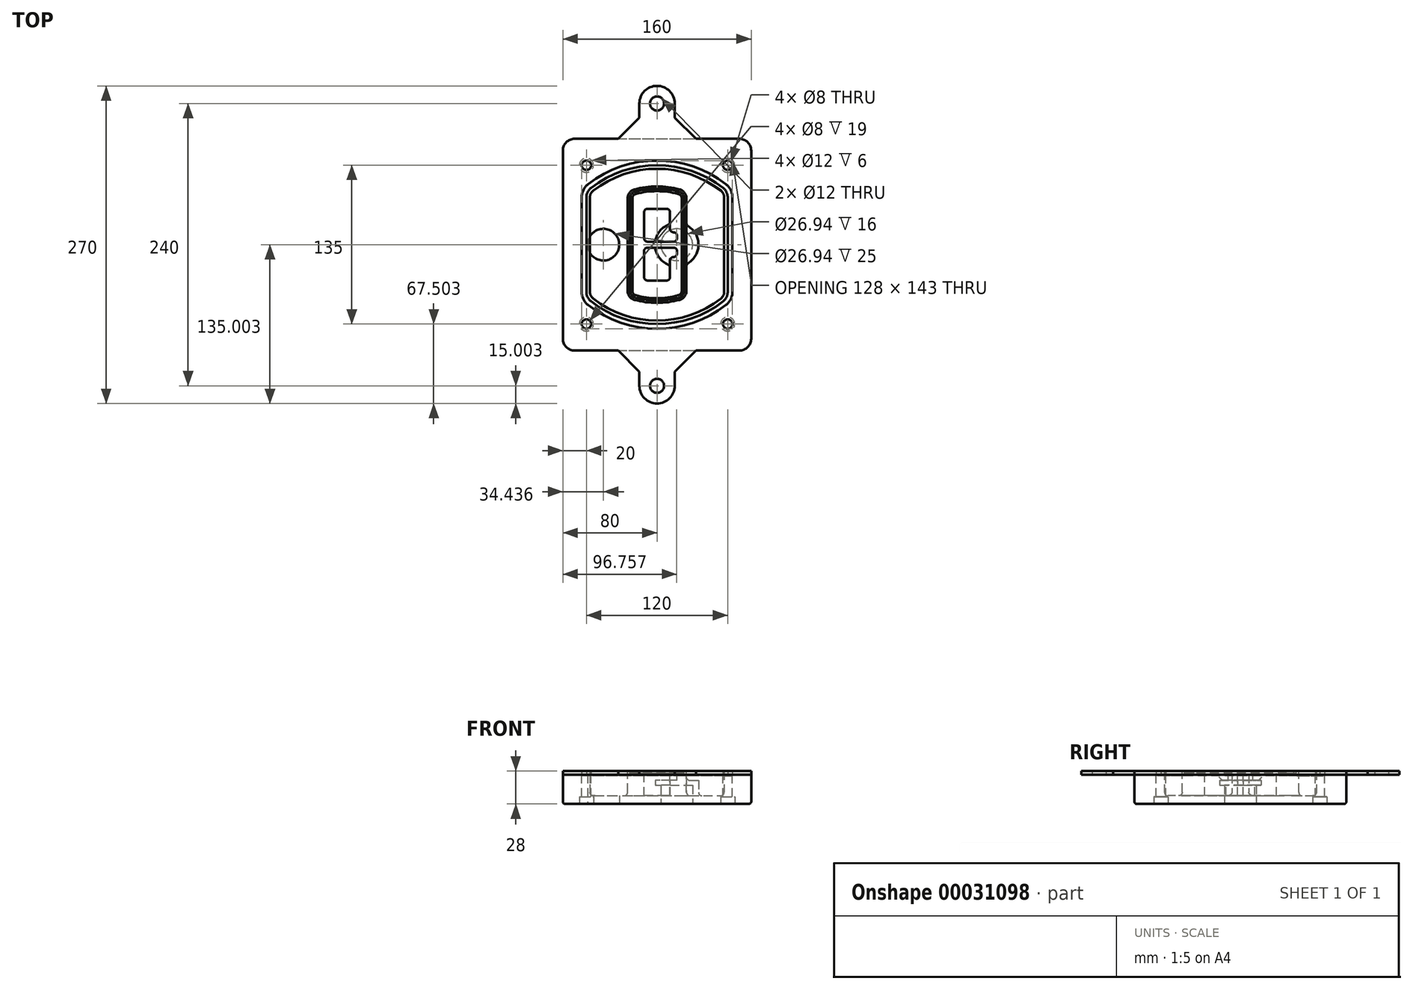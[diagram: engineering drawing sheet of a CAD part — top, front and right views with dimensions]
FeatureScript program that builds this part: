
annotation { "Feature Type Name" : "Feature", "Feature Type Description" : "" }
export const myFeature = defineFeature(function(context is Context, id is Id, definition is map)
    precondition{}
    {
        {
            var Q0;
            Q0=qCreatedBy(makeId("Top.planeOp"),FACE);
            var sketch = newSketch(context, id + "F0", { "sketchPlane" : qUnion([Q0])});
            skPoint(sketch, "E0.rect.middle", {"position": v(0, 0) * mm});
            skLineSegment(sketch, "E1.bottom", {"start": v(24.05, 28.38) * mm, "end": v(164.05, 28.38) * mm});
            skLineSegment(sketch, "E1.top", {"start": v(24.05, 208.38) * mm, "end": v(164.05, 208.38) * mm});
            skLineSegment(sketch, "E1.left", {"start": v(14.05, 38.38) * mm, "end": v(14.05, 198.38) * mm});
            skLineSegment(sketch, "E1.right", {"start": v(174.05, 38.38) * mm, "end": v(174.05, 198.38) * mm});
            skLineSegment(sketch, "E2", {"start": v(14.05, 208.38) * mm, "end": v(174.05, 28.38) * mm, "construction": true});
            skLineSegment(sketch, "E3", {"start": v(174.05, 208.38) * mm, "end": v(14.05, 28.38) * mm, "construction": true});
            skCircle(sketch, "E4", {"center": v(34.05, 185.88) * mm, "radius": 4 * mm});
            skCircle(sketch, "E5", {"center": v(154.05, 185.88) * mm, "radius": 4 * mm});
            skCircle(sketch, "E6", {"center": v(154.05, 50.88) * mm, "radius": 4 * mm});
            skCircle(sketch, "E7", {"center": v(34.05, 50.88) * mm, "radius": 4 * mm});
            skLineSegment(sketch, "E8", {"start": v(34.05, 185.88) * mm, "end": v(154.05, 185.88) * mm, "construction": true});
            skLineSegment(sketch, "E9", {"start": v(154.05, 185.88) * mm, "end": v(154.05, 50.88) * mm, "construction": true});
            skLineSegment(sketch, "E10", {"start": v(154.05, 50.88) * mm, "end": v(34.05, 50.88) * mm, "construction": true});
            skLineSegment(sketch, "E11", {"start": v(34.05, 50.88) * mm, "end": v(34.05, 185.88) * mm, "construction": true});
            skLineSegment(sketch, "E12", {"start": v(34.05, 158.68) * mm, "end": v(34.05, 78.09) * mm});
            skLineSegment(sketch, "E13", {"start": v(154.05, 158.68) * mm, "end": v(154.05, 78.09) * mm});
            skArc(sketch, "E14", {"start": v(150.2, 166.56) * mm, "mid": v(94.05, 185.88) * mm, "end": v(37.9, 166.56) * mm});
            skArc(sketch, "E15", {"start": v(37.9, 70.2) * mm, "mid": v(94.05, 50.88) * mm, "end": v(150.2, 70.2) * mm});
            skLineSegment(sketch, "E16", {"start": v(34.05, 118.38) * mm, "end": v(154.05, 118.38) * mm, "construction": true});
            skPoint(sketch, "E17.visualSharp", {"position": v(34.05, 73.38) * mm});
            skArc(sketch, "E17.filletArc", {"start": v(34.05, 78.09) * mm, "mid": v(35.06, 73.7) * mm, "end": v(37.9, 70.2) * mm});
            skPoint(sketch, "E18.visualSharp", {"position": v(34.05, 163.38) * mm});
            skArc(sketch, "E18.filletArc", {"start": v(37.9, 166.56) * mm, "mid": v(35.06, 163.06) * mm, "end": v(34.05, 158.68) * mm});
            skPoint(sketch, "E19.visualSharp", {"position": v(154.05, 163.38) * mm});
            skArc(sketch, "E19.filletArc", {"start": v(154.05, 158.68) * mm, "mid": v(153.04, 163.06) * mm, "end": v(150.2, 166.56) * mm});
            skPoint(sketch, "E20.visualSharp", {"position": v(154.05, 73.38) * mm});
            skArc(sketch, "E20.filletArc", {"start": v(150.2, 70.2) * mm, "mid": v(153.04, 73.7) * mm, "end": v(154.05, 78.09) * mm});
            skPoint(sketch, "E21.visualSharp", {"position": v(14.05, 208.38) * mm});
            skArc(sketch, "E21.filletArc", {"start": v(24.05, 208.38) * mm, "mid": v(16.98, 205.45) * mm, "end": v(14.05, 198.38) * mm});
            skPoint(sketch, "E22.visualSharp", {"position": v(174.05, 208.38) * mm});
            skArc(sketch, "E22.filletArc", {"start": v(174.05, 198.38) * mm, "mid": v(171.12, 205.45) * mm, "end": v(164.05, 208.38) * mm});
            skPoint(sketch, "E23.visualSharp", {"position": v(174.05, 28.38) * mm});
            skArc(sketch, "E23.filletArc", {"start": v(164.05, 28.38) * mm, "mid": v(171.12, 31.31) * mm, "end": v(174.05, 38.38) * mm});
            skPoint(sketch, "E24.visualSharp", {"position": v(14.05, 28.38) * mm});
            skArc(sketch, "E24.filletArc", {"start": v(14.05, 38.38) * mm, "mid": v(16.98, 31.31) * mm, "end": v(24.05, 28.38) * mm});
            skArc(sketch, "E25.0", {"start": v(151.05, 158.68) * mm, "mid": v(150.34, 161.75) * mm, "end": v(148.36, 164.2) * mm});
            skLineSegment(sketch, "E25.1", {"start": v(151.05, 158.68) * mm, "end": v(151.05, 78.09) * mm});
            skArc(sketch, "E25.2", {"start": v(148.36, 72.57) * mm, "mid": v(150.34, 75.02) * mm, "end": v(151.05, 78.09) * mm});
            skArc(sketch, "E25.3", {"start": v(39.74, 72.57) * mm, "mid": v(94.05, 53.88) * mm, "end": v(148.36, 72.57) * mm});
            skArc(sketch, "E25.4", {"start": v(37.05, 78.09) * mm, "mid": v(37.76, 75.02) * mm, "end": v(39.74, 72.57) * mm});
            skArc(sketch, "E25.5", {"start": v(148.36, 164.2) * mm, "mid": v(94.05, 182.88) * mm, "end": v(39.74, 164.2) * mm});
            skLineSegment(sketch, "E25.6", {"start": v(37.05, 158.68) * mm, "end": v(37.05, 78.09) * mm});
            skArc(sketch, "E25.7", {"start": v(39.74, 164.2) * mm, "mid": v(37.76, 161.75) * mm, "end": v(37.05, 158.68) * mm});
            skArc(sketch, "E26.0", {"start": v(35.43, 169.71) * mm, "mid": v(31.47, 164.82) * mm, "end": v(30.05, 158.68) * mm});
            skArc(sketch, "E26.1", {"start": v(152.67, 169.71) * mm, "mid": v(94.05, 189.88) * mm, "end": v(35.43, 169.71) * mm});
            skArc(sketch, "E26.2", {"start": v(158.05, 158.68) * mm, "mid": v(156.63, 164.82) * mm, "end": v(152.67, 169.71) * mm});
            skLineSegment(sketch, "E26.3", {"start": v(158.05, 158.68) * mm, "end": v(158.05, 78.09) * mm});
            skArc(sketch, "E26.4", {"start": v(152.67, 67.05) * mm, "mid": v(156.63, 71.95) * mm, "end": v(158.05, 78.09) * mm});
            skLineSegment(sketch, "E26.5", {"start": v(30.05, 158.68) * mm, "end": v(30.05, 78.09) * mm});
            skArc(sketch, "E26.6", {"start": v(35.43, 67.05) * mm, "mid": v(94.05, 46.88) * mm, "end": v(152.67, 67.05) * mm});
            skArc(sketch, "E26.7", {"start": v(30.05, 78.09) * mm, "mid": v(31.47, 71.95) * mm, "end": v(35.43, 67.05) * mm});
            skSolve(sketch);
        }
        {
            var Q0;
            Q0=makeQuery(id+"F0.imprint","IMPRINT",FACE,{"disambiguationData":[TD([[makeQuery(id+"F0.imprint","IMPRINT",EDGE,{"derivedFrom":sQuery(id+"F0.wireOp",EDGE,"E1.bottom")}),1.0]])]});
            var Q1;
            Q1=makeQuery(id+"F0.imprint","IMPRINT",FACE,{"disambiguationData":[TD([[makeQuery(id+"F0.imprint","IMPRINT",EDGE,{"derivedFrom":sQuery(id+"F0.wireOp",EDGE,"E12")}),1.0]])]});
            var Q2;
            Q2=makeQuery(id+"F0.imprint","IMPRINT",FACE,{"disambiguationData":[TD([[makeQuery(id+"F0.imprint","IMPRINT",EDGE,{"derivedFrom":sQuery(id+"F0.wireOp",EDGE,"E25.0")}),1.0]])]});
            var Q3;
            Q3=makeQuery(id+"F0.imprint","IMPRINT",FACE,{"disambiguationData":[TD([[makeQuery(id+"F0.imprint","IMPRINT",EDGE,{"derivedFrom":sQuery(id+"F0.wireOp",EDGE,"E12")}),-1.0]])]});
            extrude(context, id + "F1", {"entities" : qUnion([Q0, Q1, Q2, Q3]), "oppositeDirection" : true, "depth" : 25 * mm});
        }
        {
            var Q0;
            Q0=makeQuery(id+"F0.imprint","IMPRINT",FACE,{"disambiguationData":[TD([[makeQuery(id+"F0.imprint","IMPRINT",EDGE,{"derivedFrom":sQuery(id+"F0.wireOp",EDGE,"E12")}),1.0]])]});
            extrude(context, id + "F2", {"entities" : qUnion([Q0]), "operationType" : NewBodyOperationType.ADD, "depth" : 3 * mm});
        }
        {
            var Q0;
            Q0=makeQuery(id+"F0.imprint","IMPRINT",FACE,{"disambiguationData":[TD([[makeQuery(id+"F0.imprint","IMPRINT",EDGE,{"derivedFrom":sQuery(id+"F0.wireOp",EDGE,"E12")}),-1.0]])]});
            extrude(context, id + "F3", {"entities" : qUnion([Q0]), "operationType" : NewBodyOperationType.REMOVE, "oppositeDirection" : true, "depth" : 1 * mm});
        }
        {
            var Q0;
            Q0=makeQuery(id+"F0.imprint","IMPRINT",FACE,{"disambiguationData":[TD([[makeQuery(id+"F0.imprint","IMPRINT",EDGE,{"derivedFrom":sQuery(id+"F0.wireOp",EDGE,"E25.0")}),1.0]])]});
            extrude(context, id + "F4", {"entities" : qUnion([Q0]), "operationType" : NewBodyOperationType.REMOVE, "oppositeDirection" : true, "depth" : 18 * mm});
        }
        {
            var Q0;
            Q0=makeQuery(id+"F2.opExtrude","CAP_FACE",FACE,{"disambiguationData":[OSD([sQuery(id+"F0.wireOp",EDGE,"E12"),sQuery(id+"F0.wireOp",EDGE,"E13"),sQuery(id+"F0.wireOp",EDGE,"E14"),sQuery(id+"F0.wireOp",EDGE,"E15"),sQuery(id+"F0.wireOp",EDGE,"E17.filletArc"),sQuery(id+"F0.wireOp",EDGE,"E18.filletArc"),sQuery(id+"F0.wireOp",EDGE,"E19.filletArc"),sQuery(id+"F0.wireOp",EDGE,"E20.filletArc"),sQuery(id+"F0.wireOp",EDGE,"E25.0"),sQuery(id+"F0.wireOp",EDGE,"E25.1"),sQuery(id+"F0.wireOp",EDGE,"E25.2"),sQuery(id+"F0.wireOp",EDGE,"E25.3"),sQuery(id+"F0.wireOp",EDGE,"E25.4"),sQuery(id+"F0.wireOp",EDGE,"E25.5"),sQuery(id+"F0.wireOp",EDGE,"E25.6"),sQuery(id+"F0.wireOp",EDGE,"E25.7")])],"isStart":false});
            var sketch = newSketch(context, id + "F5", { "sketchPlane" : qUnion([Q0])});
            skArc(sketch, "E27.0", {"start": v(74.97, 71.41) * mm, "mid": v(94.05, 68.88) * mm, "end": v(113.13, 71.41) * mm});
            skArc(sketch, "E28.0", {"start": v(113.13, 165.35) * mm, "mid": v(94.05, 167.88) * mm, "end": v(74.97, 165.35) * mm});
            skLineSegment(sketch, "E29", {"start": v(69.05, 157.63) * mm, "end": v(69.05, 79.14) * mm});
            skLineSegment(sketch, "E30", {"start": v(119.05, 157.63) * mm, "end": v(119.05, 79.14) * mm});
            skLineSegment(sketch, "E31", {"start": v(69.05, 163.48) * mm, "end": v(119.05, 163.48) * mm, "construction": true});
            skLineSegment(sketch, "E32", {"start": v(69.05, 73.28) * mm, "end": v(119.05, 73.28) * mm, "construction": true});
            skPoint(sketch, "E33.visualSharp", {"position": v(69.05, 163.48) * mm});
            skArc(sketch, "E33.filletArc", {"start": v(74.97, 165.35) * mm, "mid": v(70.7, 162.5) * mm, "end": v(69.05, 157.63) * mm});
            skPoint(sketch, "E34.visualSharp", {"position": v(119.05, 163.48) * mm});
            skArc(sketch, "E34.filletArc", {"start": v(119.05, 157.63) * mm, "mid": v(117.4, 162.5) * mm, "end": v(113.13, 165.35) * mm});
            skPoint(sketch, "E35.visualSharp", {"position": v(119.05, 73.28) * mm});
            skArc(sketch, "E35.filletArc", {"start": v(113.13, 71.41) * mm, "mid": v(117.4, 74.27) * mm, "end": v(119.05, 79.14) * mm});
            skPoint(sketch, "E36.visualSharp", {"position": v(69.05, 73.28) * mm});
            skArc(sketch, "E36.filletArc", {"start": v(69.05, 79.14) * mm, "mid": v(70.7, 74.27) * mm, "end": v(74.97, 71.41) * mm});
            skArc(sketch, "E37.0", {"start": v(148.36, 164.2) * mm, "mid": v(94.05, 182.88) * mm, "end": v(39.74, 164.2) * mm});
            skArc(sketch, "E37.1", {"start": v(39.74, 164.2) * mm, "mid": v(37.76, 161.75) * mm, "end": v(37.05, 158.68) * mm});
            skLineSegment(sketch, "E37.2", {"start": v(37.05, 158.68) * mm, "end": v(37.05, 78.09) * mm});
            skArc(sketch, "E37.3", {"start": v(37.05, 78.09) * mm, "mid": v(37.76, 75.02) * mm, "end": v(39.74, 72.57) * mm});
            skArc(sketch, "E37.4", {"start": v(39.74, 72.57) * mm, "mid": v(94.05, 53.88) * mm, "end": v(148.36, 72.57) * mm});
            skArc(sketch, "E37.5", {"start": v(148.36, 72.57) * mm, "mid": v(150.34, 75.02) * mm, "end": v(151.05, 78.09) * mm});
            skLineSegment(sketch, "E37.6", {"start": v(151.05, 158.68) * mm, "end": v(151.05, 78.09) * mm});
            skArc(sketch, "E37.7", {"start": v(151.05, 158.68) * mm, "mid": v(150.34, 161.75) * mm, "end": v(148.36, 164.2) * mm});
            skLineSegment(sketch, "E38.0", {"start": v(117.05, 157.63) * mm, "end": v(117.05, 79.14) * mm});
            skArc(sketch, "E38.1", {"start": v(112.61, 73.34) * mm, "mid": v(115.81, 75.49) * mm, "end": v(117.05, 79.14) * mm});
            skArc(sketch, "E38.2", {"start": v(75.49, 73.34) * mm, "mid": v(94.05, 70.88) * mm, "end": v(112.61, 73.34) * mm});
            skArc(sketch, "E38.3", {"start": v(71.05, 79.14) * mm, "mid": v(72.29, 75.49) * mm, "end": v(75.49, 73.34) * mm});
            skLineSegment(sketch, "E38.4", {"start": v(71.05, 157.63) * mm, "end": v(71.05, 79.14) * mm});
            skArc(sketch, "E38.5", {"start": v(117.05, 157.63) * mm, "mid": v(115.81, 161.28) * mm, "end": v(112.61, 163.42) * mm});
            skArc(sketch, "E38.6", {"start": v(75.49, 163.42) * mm, "mid": v(72.29, 161.28) * mm, "end": v(71.05, 157.63) * mm});
            skArc(sketch, "E38.7", {"start": v(112.61, 163.42) * mm, "mid": v(94.05, 165.88) * mm, "end": v(75.49, 163.42) * mm});
            skArc(sketch, "E39.0", {"start": v(115.05, 157.63) * mm, "mid": v(114.23, 160.06) * mm, "end": v(112.1, 161.5) * mm});
            skLineSegment(sketch, "E39.1", {"start": v(115.05, 157.63) * mm, "end": v(115.05, 79.14) * mm});
            skArc(sketch, "E39.2", {"start": v(112.1, 75.27) * mm, "mid": v(114.23, 76.7) * mm, "end": v(115.05, 79.14) * mm});
            skArc(sketch, "E39.3", {"start": v(76, 75.27) * mm, "mid": v(94.05, 72.88) * mm, "end": v(112.1, 75.27) * mm});
            skArc(sketch, "E39.4", {"start": v(73.05, 79.14) * mm, "mid": v(73.87, 76.7) * mm, "end": v(76, 75.27) * mm});
            skArc(sketch, "E39.5", {"start": v(112.1, 161.5) * mm, "mid": v(94.05, 163.88) * mm, "end": v(76, 161.5) * mm});
            skLineSegment(sketch, "E39.6", {"start": v(73.05, 157.63) * mm, "end": v(73.05, 79.14) * mm});
            skArc(sketch, "E39.7", {"start": v(76, 161.5) * mm, "mid": v(73.87, 160.06) * mm, "end": v(73.05, 157.63) * mm});
            skLineSegment(sketch, "E40", {"start": v(69.05, 118.38) * mm, "end": v(119.05, 118.38) * mm, "construction": true});
            skLineSegment(sketch, "E41", {"start": v(83.05, 123.88) * mm, "end": v(83.05, 145.88) * mm});
            skLineSegment(sketch, "E42", {"start": v(86.05, 148.88) * mm, "end": v(102.05, 148.88) * mm});
            skLineSegment(sketch, "E43", {"start": v(105.05, 145.88) * mm, "end": v(105.05, 131.88) * mm});
            skLineSegment(sketch, "E44", {"start": v(108.05, 128.88) * mm, "end": v(108.05, 128.88) * mm});
            skLineSegment(sketch, "E45", {"start": v(111.05, 125.88) * mm, "end": v(111.05, 123.88) * mm});
            skLineSegment(sketch, "E46", {"start": v(108.05, 120.88) * mm, "end": v(86.05, 120.88) * mm});
            skPoint(sketch, "E47.visualSharp", {"position": v(83.05, 148.88) * mm});
            skArc(sketch, "E47.filletArc", {"start": v(86.05, 148.88) * mm, "mid": v(83.93, 148) * mm, "end": v(83.05, 145.88) * mm});
            skPoint(sketch, "E48.visualSharp", {"position": v(105.05, 148.88) * mm});
            skArc(sketch, "E48.filletArc", {"start": v(105.05, 145.88) * mm, "mid": v(104.17, 148) * mm, "end": v(102.05, 148.88) * mm});
            skPoint(sketch, "E49.visualSharp", {"position": v(105.05, 128.88) * mm});
            skArc(sketch, "E49.filletArc", {"start": v(105.05, 131.88) * mm, "mid": v(105.93, 129.76) * mm, "end": v(108.05, 128.88) * mm});
            skPoint(sketch, "E50.visualSharp", {"position": v(111.05, 128.88) * mm});
            skArc(sketch, "E50.filletArc", {"start": v(111.05, 125.88) * mm, "mid": v(110.17, 128) * mm, "end": v(108.05, 128.88) * mm});
            skPoint(sketch, "E51.visualSharp", {"position": v(111.05, 120.88) * mm});
            skArc(sketch, "E51.filletArc", {"start": v(108.05, 120.88) * mm, "mid": v(110.17, 121.76) * mm, "end": v(111.05, 123.88) * mm});
            skPoint(sketch, "E52.visualSharp", {"position": v(83.05, 120.88) * mm});
            skArc(sketch, "E52.filletArc", {"start": v(83.05, 123.88) * mm, "mid": v(83.93, 121.76) * mm, "end": v(86.05, 120.88) * mm});
            skLineSegment(sketch, "E53.0.MirrorCS", {"start": v(108.05, 115.88) * mm, "end": v(86.05, 115.88) * mm});
            skArc(sketch, "E54.0.MirrorCS", {"start": v(83.05, 112.88) * mm, "mid": v(83.93, 115) * mm, "end": v(86.05, 115.88) * mm});
            skLineSegment(sketch, "E55.0.MirrorCS", {"start": v(83.05, 112.88) * mm, "end": v(83.05, 90.88) * mm});
            skArc(sketch, "E56.0.MirrorCS", {"start": v(86.05, 87.88) * mm, "mid": v(83.93, 88.76) * mm, "end": v(83.05, 90.88) * mm});
            skLineSegment(sketch, "E57.0.MirrorCS", {"start": v(86.05, 87.88) * mm, "end": v(102.05, 87.88) * mm});
            skArc(sketch, "E58.0.MirrorCS", {"start": v(105.05, 90.88) * mm, "mid": v(104.17, 88.76) * mm, "end": v(102.05, 87.88) * mm});
            skLineSegment(sketch, "E59.0.MirrorCS", {"start": v(105.05, 90.88) * mm, "end": v(105.05, 104.88) * mm});
            skArc(sketch, "E60.0.MirrorCS", {"start": v(105.05, 104.88) * mm, "mid": v(105.93, 107) * mm, "end": v(108.05, 107.88) * mm});
            skArc(sketch, "E61.0.MirrorCS", {"start": v(111.05, 110.88) * mm, "mid": v(110.17, 108.76) * mm, "end": v(108.05, 107.88) * mm});
            skLineSegment(sketch, "E62.0.MirrorCS", {"start": v(111.05, 110.88) * mm, "end": v(111.05, 112.88) * mm});
            skArc(sketch, "E63.0.MirrorCS", {"start": v(108.05, 115.88) * mm, "mid": v(110.17, 115) * mm, "end": v(111.05, 112.88) * mm});
            skSolve(sketch);
        }
        {
            var Q0;
            Q0=makeQuery(id+"F5.imprint","IMPRINT",FACE,{"disambiguationData":[TD([[makeQuery(id+"F5.imprint","IMPRINT",EDGE,{"derivedFrom":sQuery(id+"F5.wireOp",EDGE,"E27.0")}),1.0]])]});
            var Q1;
            Q1=makeQuery(id+"F5.imprint","IMPRINT",FACE,{"disambiguationData":[TD([[makeQuery(id+"F5.imprint","IMPRINT",EDGE,{"derivedFrom":sQuery(id+"F5.wireOp",EDGE,"E38.0")}),-1.0]])]});
            var Q2;
            Q2=makeQuery(id+"F5.imprint","IMPRINT",FACE,{"disambiguationData":[TD([[makeQuery(id+"F5.imprint","IMPRINT",EDGE,{"derivedFrom":sQuery(id+"F5.wireOp",EDGE,"E39.0")}),1.0]])]});
            extrude(context, id + "F6", {"entities" : qUnion([Q0, Q1, Q2]), "operationType" : NewBodyOperationType.ADD, "endBound" : BoundingType.UP_TO_NEXT, "oppositeDirection" : true, "depth" : 25 * mm});
        }
        {
            var Q0;
            Q0=makeQuery(id+"F5.imprint","IMPRINT",FACE,{"disambiguationData":[TD([[makeQuery(id+"F5.imprint","IMPRINT",EDGE,{"derivedFrom":sQuery(id+"F5.wireOp",EDGE,"E38.0")}),-1.0]])]});
            extrude(context, id + "F7", {"entities" : qUnion([Q0]), "operationType" : NewBodyOperationType.REMOVE, "oppositeDirection" : true, "depth" : 2 * mm});
        }
        {
            var Q0;
            Q0=makeQuery(id+"F1.opExtrude","CAP_FACE",FACE,{"disambiguationData":[OSD([sQuery(id+"F0.wireOp",EDGE,"E1.bottom"),sQuery(id+"F0.wireOp",EDGE,"E1.top"),sQuery(id+"F0.wireOp",EDGE,"E1.left"),sQuery(id+"F0.wireOp",EDGE,"E1.right"),sQuery(id+"F0.wireOp",EDGE,"E4"),sQuery(id+"F0.wireOp",EDGE,"E5"),sQuery(id+"F0.wireOp",EDGE,"E6"),sQuery(id+"F0.wireOp",EDGE,"E7"),sQuery(id+"F0.wireOp",EDGE,"E21.filletArc"),sQuery(id+"F0.wireOp",EDGE,"E22.filletArc"),sQuery(id+"F0.wireOp",EDGE,"E23.filletArc"),sQuery(id+"F0.wireOp",EDGE,"E24.filletArc")])],"isStart":false});
            var sketch = newSketch(context, id + "F8", { "sketchPlane" : qUnion([Q0])});
            skCircle(sketch, "E64", {"center": v(110.8, -118.38) * mm, "radius": 13.47 * mm});
            skCircle(sketch, "E65", {"center": v(48.49, -118.38) * mm, "radius": 13.47 * mm});
            skLineSegment(sketch, "E66", {"start": v(174.05, -118.38) * mm, "end": v(14.05, -118.38) * mm});
            skCircle(sketch, "E67", {"center": v(110.8, -118.38) * mm, "radius": 18.47 * mm});
            skCircle(sketch, "E68", {"center": v(154.05, -185.88) * mm, "radius": 6 * mm});
            skCircle(sketch, "E69", {"center": v(34.05, -185.88) * mm, "radius": 6 * mm});
            skCircle(sketch, "E70", {"center": v(34.05, -50.88) * mm, "radius": 6 * mm});
            skCircle(sketch, "E71", {"center": v(154.05, -50.88) * mm, "radius": 6 * mm});
            skSolve(sketch);
        }
        {
            var Q0;
            {var subQ1=sQuery(id+"F8.wireOp",EDGE,"E66");var subQ4=sQuery(id+"F8.wireOp",EDGE,"E64");var subQ6=makeQuery(id+"F8.imprint","INTERSECT",VERTEX,{"disambiguationData":[OD(0.0)],"derivedFrom":[subQ4,subQ1]});Q0=makeQuery(id+"F8.imprint","IMPRINT",FACE,{"disambiguationData":[TD([[makeQuery(id+"F8.imprint","IMPRINT",EDGE,{"disambiguationData":[TD([[subQ6,-1.0]])],"derivedFrom":subQ4}),-1.0]])]});}
            var Q1;
            {var subQ0=sQuery(id+"F8.wireOp",EDGE,"E66");var subQ1=sQuery(id+"F8.wireOp",EDGE,"E64");var subQ3=makeQuery(id+"F8.imprint","INTERSECT",VERTEX,{"disambiguationData":[OD(0.0)],"derivedFrom":[subQ1,subQ0]});Q1=makeQuery(id+"F8.imprint","IMPRINT",FACE,{"disambiguationData":[TD([[makeQuery(id+"F8.imprint","IMPRINT",EDGE,{"disambiguationData":[TD([[subQ3,-1.0]])],"derivedFrom":subQ1}),1.0]])]});}
            var Q2;
            {var subQ0=sQuery(id+"F8.wireOp",EDGE,"E66");var subQ1=sQuery(id+"F8.wireOp",EDGE,"E64");var subQ3=makeQuery(id+"F8.imprint","INTERSECT",VERTEX,{"disambiguationData":[OD(0.0)],"derivedFrom":[subQ1,subQ0]});Q2=makeQuery(id+"F8.imprint","IMPRINT",FACE,{"disambiguationData":[TD([[makeQuery(id+"F8.imprint","IMPRINT",EDGE,{"disambiguationData":[TD([[subQ3,1.0]])],"derivedFrom":subQ1}),1.0]])]});}
            var Q3;
            {var subQ1=sQuery(id+"F8.wireOp",EDGE,"E66");var subQ4=sQuery(id+"F8.wireOp",EDGE,"E64");var subQ6=makeQuery(id+"F8.imprint","INTERSECT",VERTEX,{"disambiguationData":[OD(0.0)],"derivedFrom":[subQ4,subQ1]});Q3=makeQuery(id+"F8.imprint","IMPRINT",FACE,{"disambiguationData":[TD([[makeQuery(id+"F8.imprint","IMPRINT",EDGE,{"disambiguationData":[TD([[subQ6,1.0]])],"derivedFrom":subQ4}),-1.0]])]});}
            extrude(context, id + "F9", {"entities" : qUnion([Q0, Q1, Q2, Q3]), "operationType" : NewBodyOperationType.ADD, "oppositeDirection" : true, "depth" : 20 * mm});
        }
        {
            var Q0;
            {var subQ0=sQuery(id+"F8.wireOp",EDGE,"E66");var subQ1=sQuery(id+"F8.wireOp",EDGE,"E64");var subQ3=makeQuery(id+"F8.imprint","INTERSECT",VERTEX,{"disambiguationData":[OD(0.0)],"derivedFrom":[subQ1,subQ0]});Q0=makeQuery(id+"F8.imprint","IMPRINT",FACE,{"disambiguationData":[TD([[makeQuery(id+"F8.imprint","IMPRINT",EDGE,{"disambiguationData":[TD([[subQ3,-1.0]])],"derivedFrom":subQ1}),1.0]])]});}
            var Q1;
            {var subQ0=sQuery(id+"F8.wireOp",EDGE,"E66");var subQ1=sQuery(id+"F8.wireOp",EDGE,"E64");var subQ3=makeQuery(id+"F8.imprint","INTERSECT",VERTEX,{"disambiguationData":[OD(0.0)],"derivedFrom":[subQ1,subQ0]});Q1=makeQuery(id+"F8.imprint","IMPRINT",FACE,{"disambiguationData":[TD([[makeQuery(id+"F8.imprint","IMPRINT",EDGE,{"disambiguationData":[TD([[subQ3,1.0]])],"derivedFrom":subQ1}),1.0]])]});}
            extrude(context, id + "F10", {"entities" : qUnion([Q0, Q1]), "operationType" : NewBodyOperationType.REMOVE, "oppositeDirection" : true, "depth" : 16 * mm});
        }
        {
            var Q0;
            {var subQ0=sQuery(id+"F8.wireOp",EDGE,"E66");var subQ1=sQuery(id+"F8.wireOp",EDGE,"E65");var subQ3=makeQuery(id+"F8.imprint","INTERSECT",VERTEX,{"disambiguationData":[OD(0.0)],"derivedFrom":[subQ1,subQ0]});Q0=makeQuery(id+"F8.imprint","IMPRINT",FACE,{"disambiguationData":[TD([[makeQuery(id+"F8.imprint","IMPRINT",EDGE,{"disambiguationData":[TD([[subQ3,-1.0]])],"derivedFrom":subQ1}),1.0]])]});}
            var Q1;
            {var subQ0=sQuery(id+"F8.wireOp",EDGE,"E66");var subQ1=sQuery(id+"F8.wireOp",EDGE,"E65");var subQ3=makeQuery(id+"F8.imprint","INTERSECT",VERTEX,{"disambiguationData":[OD(0.0)],"derivedFrom":[subQ1,subQ0]});Q1=makeQuery(id+"F8.imprint","IMPRINT",FACE,{"disambiguationData":[TD([[makeQuery(id+"F8.imprint","IMPRINT",EDGE,{"disambiguationData":[TD([[subQ3,1.0]])],"derivedFrom":subQ1}),1.0]])]});}
            extrude(context, id + "F11", {"entities" : qUnion([Q0, Q1]), "operationType" : NewBodyOperationType.REMOVE, "oppositeDirection" : true, "depth" : 25 * mm});
        }
        {
            var Q0;
            Q0=makeQuery(id+"F8.imprint","IMPRINT",FACE,{"disambiguationData":[TD([[makeQuery(id+"F8.imprint","IMPRINT",EDGE,{"derivedFrom":sQuery(id+"F8.wireOp",EDGE,"E68")}),1.0]])]});
            var Q1;
            Q1=makeQuery(id+"F8.imprint","IMPRINT",FACE,{"disambiguationData":[TD([[makeQuery(id+"F8.imprint","IMPRINT",EDGE,{"derivedFrom":makeQuery(id+"F1.opExtrude","CAP_EDGE",EDGE,{"disambiguationData":[OSD([sQuery(id+"F0.wireOp",EDGE,"E5")])],"isStart":false})}),-1.0]])]});
            var Q2;
            Q2=makeQuery(id+"F8.imprint","IMPRINT",FACE,{"disambiguationData":[TD([[makeQuery(id+"F8.imprint","IMPRINT",EDGE,{"derivedFrom":sQuery(id+"F8.wireOp",EDGE,"E69")}),1.0]])]});
            var Q3;
            Q3=makeQuery(id+"F8.imprint","IMPRINT",FACE,{"disambiguationData":[TD([[makeQuery(id+"F8.imprint","IMPRINT",EDGE,{"derivedFrom":makeQuery(id+"F1.opExtrude","CAP_EDGE",EDGE,{"disambiguationData":[OSD([sQuery(id+"F0.wireOp",EDGE,"E4")])],"isStart":false})}),-1.0]])]});
            var Q4;
            Q4=makeQuery(id+"F8.imprint","IMPRINT",FACE,{"disambiguationData":[TD([[makeQuery(id+"F8.imprint","IMPRINT",EDGE,{"derivedFrom":sQuery(id+"F8.wireOp",EDGE,"E70")}),1.0]])]});
            var Q5;
            Q5=makeQuery(id+"F8.imprint","IMPRINT",FACE,{"disambiguationData":[TD([[makeQuery(id+"F8.imprint","IMPRINT",EDGE,{"derivedFrom":makeQuery(id+"F1.opExtrude","CAP_EDGE",EDGE,{"disambiguationData":[OSD([sQuery(id+"F0.wireOp",EDGE,"E7")])],"isStart":false})}),-1.0]])]});
            var Q6;
            Q6=makeQuery(id+"F8.imprint","IMPRINT",FACE,{"disambiguationData":[TD([[makeQuery(id+"F8.imprint","IMPRINT",EDGE,{"derivedFrom":sQuery(id+"F8.wireOp",EDGE,"E71")}),1.0]])]});
            var Q7;
            Q7=makeQuery(id+"F8.imprint","IMPRINT",FACE,{"disambiguationData":[TD([[makeQuery(id+"F8.imprint","IMPRINT",EDGE,{"derivedFrom":makeQuery(id+"F1.opExtrude","CAP_EDGE",EDGE,{"disambiguationData":[OSD([sQuery(id+"F0.wireOp",EDGE,"E6")])],"isStart":false})}),-1.0]])]});
            extrude(context, id + "F12", {"entities" : qUnion([Q0, Q1, Q2, Q3, Q4, Q5, Q6, Q7]), "operationType" : NewBodyOperationType.REMOVE, "oppositeDirection" : true, "depth" : 6 * mm});
        }
        {
            var Q0;
            Q0=makeQuery(id+"F10.boolean.opBoolean","COPY",FACE,{"derivedFrom":makeQuery(id+"F10.opExtrude","CAP_FACE",FACE,{"disambiguationData":[OSD([sQuery(id+"F8.wireOp",EDGE,"E64")])],"isStart":false})});
            var sketch = newSketch(context, id + "F13", { "sketchPlane" : qUnion([Q0])});
            skArc(sketch, "E72.0", {"start": v(105.05, -100.83) * mm, "mid": v(96.62, -106.56) * mm, "end": v(92.5, -115.88) * mm});
            skArc(sketch, "E72.1", {"start": v(92.5, -120.88) * mm, "mid": v(96.62, -130.2) * mm, "end": v(105.05, -135.93) * mm});
            skLineSegment(sketch, "E73", {"start": v(92.5, -120.88) * mm, "end": v(108.05, -120.88) * mm});
            skLineSegment(sketch, "E74.0", {"start": v(108.05, -115.88) * mm, "end": v(92.5, -115.88) * mm});
            skArc(sketch, "E74.1", {"start": v(108.05, -115.88) * mm, "mid": v(110.17, -115) * mm, "end": v(111.05, -112.88) * mm});
            skLineSegment(sketch, "E74.2", {"start": v(111.05, -110.88) * mm, "end": v(111.05, -112.88) * mm});
            skArc(sketch, "E74.3", {"start": v(111.05, -110.88) * mm, "mid": v(110.17, -108.76) * mm, "end": v(108.05, -107.88) * mm});
            skArc(sketch, "E74.4", {"start": v(105.05, -104.88) * mm, "mid": v(105.93, -107) * mm, "end": v(108.05, -107.88) * mm});
            skLineSegment(sketch, "E74.5", {"start": v(105.05, -100.83) * mm, "end": v(105.05, -104.88) * mm});
            skLineSegment(sketch, "E74.7", {"start": v(108.05, -120.88) * mm, "end": v(92.5, -120.88) * mm});
            skArc(sketch, "E74.8", {"start": v(108.05, -120.88) * mm, "mid": v(110.17, -121.76) * mm, "end": v(111.05, -123.88) * mm});
            skLineSegment(sketch, "E74.9", {"start": v(111.05, -125.88) * mm, "end": v(111.05, -123.88) * mm});
            skArc(sketch, "E74.10", {"start": v(111.05, -125.88) * mm, "mid": v(110.17, -128) * mm, "end": v(108.05, -128.88) * mm});
            skArc(sketch, "E74.11", {"start": v(105.05, -131.88) * mm, "mid": v(105.93, -129.76) * mm, "end": v(108.05, -128.88) * mm});
            skLineSegment(sketch, "E74.12", {"start": v(105.05, -135.93) * mm, "end": v(105.05, -131.88) * mm});
            skPoint(sketch, "E75.orphan", {"position": v(105.05, -145.88) * mm});
            skPoint(sketch, "E76.orphan", {"position": v(86.05, -120.88) * mm});
            skPoint(sketch, "E77.orphan", {"position": v(86.05, -115.88) * mm});
            skPoint(sketch, "E78.orphan", {"position": v(105.05, -90.88) * mm});
            skSolve(sketch);
        }
        {
            var Q0;
            {var subQ7=sQuery(id+"F13.wireOp",EDGE,"E72.0");var subQ14=sQuery(id+"F13.wireOp",EDGE,"E72.1");var subQ16=sQuery(id+"F13.wireOp",EDGE,"E74.1");var subQ18=sQuery(id+"F13.wireOp",EDGE,"E74.8");Q0=qUnion([makeQuery(id+"F13.imprint","IMPRINT",FACE,{"disambiguationData":[TD([[makeQuery(id+"F13.imprint","IMPRINT",EDGE,{"derivedFrom":subQ7}),1.0]])]}),makeQuery(id+"F13.imprint","IMPRINT",FACE,{"disambiguationData":[TD([[makeQuery(id+"F13.imprint","IMPRINT",EDGE,{"derivedFrom":subQ14}),1.0]])]}),makeQuery(id+"F13.imprint","IMPRINT",FACE,{"disambiguationData":[TD([[makeQuery(id+"F13.imprint","IMPRINT",EDGE,{"derivedFrom":subQ16}),1.0]])]}),makeQuery(id+"F13.imprint","IMPRINT",FACE,{"disambiguationData":[TD([[makeQuery(id+"F13.imprint","IMPRINT",EDGE,{"derivedFrom":subQ18}),-1.0]])]})]);}
            var Q1;
            Q1=makeQuery(id+"F6.boolean.opBoolean","SPLIT",FACE,{"disambiguationData":[TD([makeQuery(id+"F6.opExtrude","SWEPT_FACE",FACE,{"disambiguationData":[OSD([sQuery(id+"F5.wireOp",EDGE,"E41")])]})])],"derivedFrom":makeQuery(id+"F4.boolean.opBoolean","COPY",FACE,{"derivedFrom":makeQuery(id+"F4.opExtrude","CAP_FACE",FACE,{"disambiguationData":[OSD([sQuery(id+"F0.wireOp",EDGE,"E25.0"),sQuery(id+"F0.wireOp",EDGE,"E25.1"),sQuery(id+"F0.wireOp",EDGE,"E25.2"),sQuery(id+"F0.wireOp",EDGE,"E25.3"),sQuery(id+"F0.wireOp",EDGE,"E25.4"),sQuery(id+"F0.wireOp",EDGE,"E25.5"),sQuery(id+"F0.wireOp",EDGE,"E25.6"),sQuery(id+"F0.wireOp",EDGE,"E25.7")])],"isStart":false})})});
            extrude(context, id + "F14", {"entities" : qUnion([Q0]), "operationType" : NewBodyOperationType.REMOVE, "endBound" : BoundingType.UP_TO_SURFACE, "endBoundEntityFace" : qUnion([Q1]), "depth" : 25 * mm});
        }
        {
            var Q0;
            Q0=makeQuery(id+"F4.boolean.opBoolean","COPY",EDGE,{"derivedFrom":makeQuery(id+"F4.opExtrude","CAP_EDGE",EDGE,{"disambiguationData":[OSD([sQuery(id+"F0.wireOp",EDGE,"E25.6")])],"isStart":false})});
            var Q1;
            Q1=makeQuery(id+"F9.boolean.opBoolean","INTERSECT",EDGE,{"derivedFrom":[makeQuery(id+"F6.opExtrude","SWEPT_FACE",FACE,{"disambiguationData":[OSD([sQuery(id+"F5.wireOp",EDGE,"E30")])]}),makeQuery(id+"F9.opExtrude","CAP_FACE",FACE,{"disambiguationData":[OSD([sQuery(id+"F8.wireOp",EDGE,"E67")])],"isStart":false})]});
            var Q2;
            Q2=makeQuery(id+"F9.boolean.opBoolean","INTERSECT",EDGE,{"disambiguationData":[OD(1.0)],"derivedFrom":[makeQuery(id+"F6.opExtrude","SWEPT_FACE",FACE,{"disambiguationData":[OSD([sQuery(id+"F5.wireOp",EDGE,"E30")])]}),makeQuery(id+"F9.opExtrude","SWEPT_FACE",FACE,{"disambiguationData":[OSD([sQuery(id+"F8.wireOp",EDGE,"E67")])]})]});
            var Q3;
            {var subQ0=sQuery(id+"F5.wireOp",EDGE,"E30");Q3=makeQuery(id+"F9.boolean.opBoolean","SPLIT",EDGE,{"disambiguationData":[TD([makeQuery(id+"F6.opExtrude","SWEPT_FACE",FACE,{"disambiguationData":[OSD([sQuery(id+"F5.wireOp",EDGE,"E35.filletArc")])]})])],"derivedFrom":makeQuery(id+"F6.opExtrude","CAP_EDGE",EDGE,{"disambiguationData":[OSD([subQ0])],"isStart":false})});}
            var Q4;
            {var subQ0=sQuery(id+"F0.wireOp",EDGE,"E25.7");var subQ1=sQuery(id+"F0.wireOp",EDGE,"E25.6");var subQ2=sQuery(id+"F0.wireOp",EDGE,"E25.5");var subQ3=sQuery(id+"F0.wireOp",EDGE,"E25.4");var subQ4=sQuery(id+"F0.wireOp",EDGE,"E25.0");var subQ5=sQuery(id+"F0.wireOp",EDGE,"E25.1");var subQ6=sQuery(id+"F0.wireOp",EDGE,"E25.2");var subQ7=sQuery(id+"F0.wireOp",EDGE,"E25.3");Q4=makeQuery(id+"F9.boolean.opBoolean","INTERSECT",EDGE,{"derivedFrom":[makeQuery(id+"F6.boolean.opBoolean","SPLIT",FACE,{"disambiguationData":[TD([makeQuery(id+"F2.opExtrude","SWEPT_FACE",FACE,{"disambiguationData":[OSD([subQ4])]})])],"derivedFrom":makeQuery(id+"F4.boolean.opBoolean","COPY",FACE,{"derivedFrom":makeQuery(id+"F4.opExtrude","CAP_FACE",FACE,{"disambiguationData":[OSD([subQ4,subQ5,subQ6,subQ7,subQ3,subQ2,subQ1,subQ0])],"isStart":false})})}),makeQuery(id+"F9.opExtrude","SWEPT_FACE",FACE,{"disambiguationData":[OSD([sQuery(id+"F8.wireOp",EDGE,"E67")])]})]});}
            var Q5;
            Q5=makeQuery(id+"F9.boolean.opBoolean","INTERSECT",EDGE,{"disambiguationData":[OD(0.0)],"derivedFrom":[makeQuery(id+"F6.opExtrude","SWEPT_FACE",FACE,{"disambiguationData":[OSD([sQuery(id+"F5.wireOp",EDGE,"E30")])]}),makeQuery(id+"F9.opExtrude","SWEPT_FACE",FACE,{"disambiguationData":[OSD([sQuery(id+"F8.wireOp",EDGE,"E67")])]})]});
            fillet(context, id + "F15", {"entities" : qUnion([Q0, Q1, Q2, Q3, Q4, Q5]), "radius" : 3 * mm, "tangentPropagation" : true, "allowEdgeOverflow" : false});
        }
        {
            var Q0;
            Q0=makeQuery(id+"F1.opExtrude","CAP_EDGE",EDGE,{"disambiguationData":[OSD([sQuery(id+"F0.wireOp",EDGE,"E1.bottom")])],"isStart":false});
            fillet(context, id + "F16", {"entities" : qUnion([Q0]), "radius" : 2 * mm, "tangentPropagation" : true, "allowEdgeOverflow" : false});
        }
        {
            var Q0;
            {var subQ0=sQuery(id+"F0.wireOp",EDGE,"E1.bottom");var subQ1=sQuery(id+"F0.wireOp",EDGE,"E1.top");var subQ2=sQuery(id+"F0.wireOp",EDGE,"E1.left");var subQ3=sQuery(id+"F0.wireOp",EDGE,"E1.right");var subQ4=sQuery(id+"F0.wireOp",EDGE,"E4");var subQ5=sQuery(id+"F0.wireOp",EDGE,"E5");var subQ6=sQuery(id+"F0.wireOp",EDGE,"E6");var subQ7=sQuery(id+"F0.wireOp",EDGE,"E7");var subQ8=sQuery(id+"F0.wireOp",EDGE,"E21.filletArc");var subQ9=sQuery(id+"F0.wireOp",EDGE,"E22.filletArc");var subQ10=sQuery(id+"F0.wireOp",EDGE,"E23.filletArc");var subQ11=sQuery(id+"F0.wireOp",EDGE,"E24.filletArc");Q0=makeQuery(id+"F2.boolean.opBoolean","SPLIT",FACE,{"disambiguationData":[TD([makeQuery(id+"F1.opExtrude","SWEPT_FACE",FACE,{"disambiguationData":[OSD([subQ0])]})])],"derivedFrom":makeQuery(id+"F1.opExtrude","CAP_FACE",FACE,{"disambiguationData":[OSD([subQ0,subQ1,subQ2,subQ3,subQ4,subQ5,subQ6,subQ7,subQ8,subQ9,subQ10,subQ11])],"isStart":true})});}
            var sketch = newSketch(context, id + "F17", { "sketchPlane" : qUnion([Q0])});
            skLineSegment(sketch, "E79.0", {"start": v(14.05, 38.38) * mm, "end": v(14.05, 198.38) * mm});
            skArc(sketch, "E79.1", {"start": v(24.05, 208.38) * mm, "mid": v(16.98, 205.45) * mm, "end": v(14.05, 198.38) * mm});
            skLineSegment(sketch, "E79.2", {"start": v(24.05, 208.38) * mm, "end": v(164.05, 208.38) * mm});
            skArc(sketch, "E79.3", {"start": v(174.05, 198.38) * mm, "mid": v(171.12, 205.45) * mm, "end": v(164.05, 208.38) * mm});
            skLineSegment(sketch, "E79.4", {"start": v(174.05, 38.38) * mm, "end": v(174.05, 198.38) * mm});
            skArc(sketch, "E79.5", {"start": v(164.05, 28.38) * mm, "mid": v(171.12, 31.31) * mm, "end": v(174.05, 38.38) * mm});
            skLineSegment(sketch, "E79.6", {"start": v(24.05, 28.38) * mm, "end": v(164.05, 28.38) * mm});
            skArc(sketch, "E79.7", {"start": v(14.05, 38.38) * mm, "mid": v(16.98, 31.31) * mm, "end": v(24.05, 28.38) * mm});
            skCircle(sketch, "E79.8", {"center": v(34.05, 50.88) * mm, "radius": 4 * mm});
            skCircle(sketch, "E79.9", {"center": v(154.05, 50.88) * mm, "radius": 4 * mm});
            skCircle(sketch, "E79.10", {"center": v(154.05, 185.88) * mm, "radius": 4 * mm});
            skCircle(sketch, "E79.11", {"center": v(34.05, 185.88) * mm, "radius": 4 * mm});
            skArc(sketch, "E79.12", {"start": v(150.2, 166.56) * mm, "mid": v(94.05, 185.88) * mm, "end": v(37.9, 166.56) * mm});
            skArc(sketch, "E79.13", {"start": v(37.9, 166.56) * mm, "mid": v(35.06, 163.06) * mm, "end": v(34.05, 158.68) * mm});
            skLineSegment(sketch, "E79.14", {"start": v(34.05, 158.68) * mm, "end": v(34.05, 78.09) * mm});
            skArc(sketch, "E79.15", {"start": v(34.05, 78.09) * mm, "mid": v(35.06, 73.7) * mm, "end": v(37.9, 70.2) * mm});
            skArc(sketch, "E79.16", {"start": v(37.9, 70.2) * mm, "mid": v(94.05, 50.88) * mm, "end": v(150.2, 70.2) * mm});
            skArc(sketch, "E79.17", {"start": v(150.2, 70.2) * mm, "mid": v(153.04, 73.7) * mm, "end": v(154.05, 78.09) * mm});
            skLineSegment(sketch, "E79.18", {"start": v(154.05, 158.68) * mm, "end": v(154.05, 78.09) * mm});
            skArc(sketch, "E79.19", {"start": v(154.05, 158.68) * mm, "mid": v(153.04, 163.06) * mm, "end": v(150.2, 166.56) * mm});
            skLineSegment(sketch, "E80", {"start": v(94.05, 208.38) * mm, "end": v(94.05, 238.38) * mm, "construction": true});
            skCircle(sketch, "E81", {"center": v(94.05, 238.38) * mm, "radius": 6 * mm});
            skLineSegment(sketch, "E82", {"start": v(79.05, 238.38) * mm, "end": v(79.05, 226.38) * mm});
            skLineSegment(sketch, "E83", {"start": v(109.05, 238.38) * mm, "end": v(109.05, 226.38) * mm});
            skLineSegment(sketch, "E84", {"start": v(79.05, 226.38) * mm, "end": v(61.05, 208.38) * mm});
            skArc(sketch, "E85", {"start": v(109.05, 238.38) * mm, "mid": v(94.05, 253.38) * mm, "end": v(79.05, 238.38) * mm});
            skLineSegment(sketch, "E86", {"start": v(109.05, 226.38) * mm, "end": v(127.05, 208.38) * mm});
            skLineSegment(sketch, "E87", {"start": v(14.05, 118.38) * mm, "end": v(203.09, 118.38) * mm, "construction": true});
            skArc(sketch, "E88.MirrorCS", {"start": v(79.05, 238.38) * mm, "mid": v(94.05, 253.38) * mm, "end": v(109.05, 238.38) * mm});
            skLineSegment(sketch, "E89.MirrorCS", {"start": v(79.05, 10.38) * mm, "end": v(61.05, 28.38) * mm});
            skLineSegment(sketch, "E90.MirrorCS", {"start": v(79.05, -1.62) * mm, "end": v(79.05, 10.38) * mm});
            skArc(sketch, "E91.MirrorCS", {"start": v(109.05, -1.62) * mm, "mid": v(94.05, -16.62) * mm, "end": v(79.05, -1.62) * mm});
            skLineSegment(sketch, "E92.MirrorCS", {"start": v(109.05, -1.62) * mm, "end": v(109.05, 10.38) * mm});
            skLineSegment(sketch, "E93.MirrorCS", {"start": v(109.05, 10.38) * mm, "end": v(127.05, 28.38) * mm});
            skCircle(sketch, "E94.MirrorC", {"center": v(94.05, -1.62) * mm, "radius": 6 * mm});
            skSolve(sketch);
        }
        {
            var Q0;
            Q0=makeQuery(id+"F17.imprint","IMPRINT",FACE,{"disambiguationData":[TD([[makeQuery(id+"F17.imprint","IMPRINT",EDGE,{"derivedFrom":sQuery(id+"F17.wireOp",EDGE,"E82")}),1.0]])]});
            var Q1;
            Q1=makeQuery(id+"F17.imprint","IMPRINT",FACE,{"disambiguationData":[TD([[makeQuery(id+"F17.imprint","IMPRINT",EDGE,{"derivedFrom":sQuery(id+"F17.wireOp",EDGE,"E79.0")}),-1.0]])]});
            var Q2;
            {var subQ1=sQuery(id+"F17.wireOp",EDGE,"E89.MirrorCS");Q2=makeQuery(id+"F17.imprint","IMPRINT",FACE,{"disambiguationData":[TD([[makeQuery(id+"F17.imprint","IMPRINT",EDGE,{"derivedFrom":subQ1}),-1.0]])]});}
            var Q3;
            Q3=makeQuery(id+"F2.opExtrude","CAP_FACE",FACE,{"disambiguationData":[OSD([sQuery(id+"F0.wireOp",EDGE,"E12"),sQuery(id+"F0.wireOp",EDGE,"E13"),sQuery(id+"F0.wireOp",EDGE,"E14"),sQuery(id+"F0.wireOp",EDGE,"E15"),sQuery(id+"F0.wireOp",EDGE,"E17.filletArc"),sQuery(id+"F0.wireOp",EDGE,"E18.filletArc"),sQuery(id+"F0.wireOp",EDGE,"E19.filletArc"),sQuery(id+"F0.wireOp",EDGE,"E20.filletArc"),sQuery(id+"F0.wireOp",EDGE,"E25.0"),sQuery(id+"F0.wireOp",EDGE,"E25.1"),sQuery(id+"F0.wireOp",EDGE,"E25.2"),sQuery(id+"F0.wireOp",EDGE,"E25.3"),sQuery(id+"F0.wireOp",EDGE,"E25.4"),sQuery(id+"F0.wireOp",EDGE,"E25.5"),sQuery(id+"F0.wireOp",EDGE,"E25.6"),sQuery(id+"F0.wireOp",EDGE,"E25.7")])],"isStart":false});
            extrude(context, id + "F18", {"entities" : qUnion([Q0, Q1, Q2]), "endBound" : BoundingType.UP_TO_SURFACE, "endBoundEntityFace" : qUnion([Q3]), "depth" : 25 * mm});
        }
    });
